# Revit family: 32-70-003-DN50-300
name_source: partatom
category: Pipe Accessories
units: mm (PartAtom-declared; Revit-internal decimal feet)

## family parameters
Always vertical = No
Cut with Voids When Loaded = No
Part Type = Valve - Breaks Into
Round Connector Dimension = Use Diameter
Shared = No
Work Plane-Based = No

## types (10) — shared parameters
32-050-70-016 = DN050_PN16
32-060-70-016 = DN060_PN16
32-065-70-016 = DN065_PN16
32-080-70-0146499 = DN080_PN16
32-100-70-0146499 = DN100_PN16
32-125-70-0146499 = DN125_PN16
32-150-70-0146499 = DN150_PN16
32-200-70-0146499 = DN200_PN16
32-250-70-016 = DN250_PN16
32-300-70-016 = DN300_PN16
Body_Wallthickness = 15 mm  [stored 0.0492126 ft]
Description_ = AVK GATE VALVE, SHORT SPIGOT ENDS
Ftc = 4 mm  [stored 0.0131234 ft]
Name_Height_reference = 10 mm  [stored 0.0328084 ft]
Rib_Height_Reference_3 = 100 mm
Rib_Thickness = 18 mm  [stored 0.0590551 ft]
Search_table = 32-70-003-DN50-300
URL product pages = https://www.avkvalves.com
zero-valued in all types: Bottom_Reference, E

## per-type parameters (varying)
- DN080_PN16: At=70 mm; Body_Height=132 mm; Body_depth=140 mm; Body_width=75 mm; Body_width_ref=90 mm; Bonnet_Flange_Depth=171 mm; Bonnet_Flange_Width=90 mm; Bonnet_Flange_cut=8 mm  [stored 0.0262467 ft]; Bonnet_Flange_thickness=15 mm  [stored 0.0492126 ft]; Bonnet_Height=50 mm; Bonnet_Reference_height=122 mm; Bonnet_Thickness=77 mm; Bt=77 mm; Bt_2=69 mm; CL _Thickness=27 mm  [stored 0.0885827 ft]; CL_Height=75 mm; Cut_Reference=560 mm; D=49 mm; D2=34 mm  [stored 0.111549 ft]; D_ref=50 mm; D_ref_2=46 mm; F=9 mm; F1=10 mm  [stored 0.0328084 ft]; F1_ref=20 mm  [stored 0.0656168 ft]; Fillet_Thickness=6 mm  [stored 0.019685 ft]; Flange_OR=100 mm; Flange_Thickness=19 mm  [stored 0.062336 ft]; Flange_Thickness_cut=30 mm  [stored 0.0984252 ft]; Ftc_reference_height=100 mm; H=282 mm; H1=248 mm; H3=337 mm; H3_ref=55 mm; Horizontal_Flange_width=110 mm; ID=40 mm  [stored 0.131234 ft]; L=280 mm; L1=85 mm; L2=140 mm; L_Dia=80 mm; L_ref=140 mm; Name_Reference=90 mm; Name_Width=38 mm; Neck_H=41 mm  [stored 0.134514 ft]; Neck_T=25 mm  [stored 0.082021 ft]; Neck_T2=23 mm  [stored 0.0754593 ft]; Nominal Diameter (DN)=80 mm; R1tv=1000 mm; R2f=15 mm  [stored 0.0492126 ft]; RF_Dia=66 mm; Rf=183 mm; Rib_Height_Reference_1=120 mm; Rib_Height_Reference_2=110 mm; Rib_Height_Reference_4=85 mm; Rib_Width_1=38 mm; Rib_Width_2=38 mm; Rib_Width_3=38 mm; Rib_depth_1=38 mm; Rib_depth_2=38 mm; Rib_depth_3=38 mm; Rt=333 mm; S=3 mm  [stored 0.00984252 ft]
- DN050_PN16: At=48 mm; Body_Height=101 mm; Body_depth=95 mm; Body_width=72 mm; Body_width_ref=86 mm; Bonnet_Flange_Depth=118 mm; Bonnet_Flange_Width=82 mm; Bonnet_Flange_cut=8 mm  [stored 0.0262467 ft]; Bonnet_Flange_thickness=15 mm  [stored 0.0492126 ft]; Bonnet_Height=41 mm  [stored 0.134514 ft]; Bonnet_Reference_height=91 mm; Bonnet_Thickness=73 mm; Bt=73 mm; Bt_2=66 mm; CL _Thickness=25 mm  [stored 0.082021 ft]; CL_Height=53 mm; Cut_Reference=488 mm; D=33 mm  [stored 0.108268 ft]; D2=29 mm  [stored 0.0951444 ft]; D_ref=35 mm  [stored 0.114829 ft]; D_ref_2=30 mm  [stored 0.0984252 ft]; F=7 mm  [stored 0.0229659 ft]; F1=9 mm; F1_ref=17 mm  [stored 0.0557743 ft]; Fillet_Thickness=6 mm  [stored 0.019685 ft]; Flange_OR=83 mm; Flange_Thickness=19 mm  [stored 0.062336 ft]; Flange_Thickness_cut=29 mm  [stored 0.0951444 ft]; Ftc_reference_height=83 mm; H=241 mm; H1=212 mm; H3=274 mm; H3_ref=33 mm  [stored 0.108268 ft]; Horizontal_Flange_width=66 mm; ID=25 mm  [stored 0.082021 ft]; L=244 mm; L1=72 mm; L2=110 mm; L_Dia=50 mm; L_ref=122 mm; Name_Reference=71 mm; Name_Width=36 mm  [stored 0.11811 ft]; Neck_H=59 mm; Neck_T=23 mm  [stored 0.0754593 ft]; Neck_T2=21 mm; Nominal Diameter (DN)=50 mm; R1tv=825 mm; R2f=15 mm  [stored 0.0492126 ft]; RF_Dia=50 mm; Rf=110 mm; Rib_Height_Reference_1=120 mm; Rib_Height_Reference_2=110 mm; Rib_Height_Reference_4=60 mm; Rib_Width_1=36 mm  [stored 0.11811 ft]; Rib_Width_2=36 mm  [stored 0.11811 ft]; Rib_Width_3=36 mm  [stored 0.11811 ft]; Rib_depth_1=36 mm  [stored 0.11811 ft]; Rib_depth_2=36 mm  [stored 0.11811 ft]; Rib_depth_3=36 mm  [stored 0.11811 ft]; Rt=275 mm; S=3 mm  [stored 0.00984252 ft]
- DN060_PN16: At=50 mm; Body_Height=110 mm; Body_depth=100 mm; Body_width=72 mm; Body_width_ref=86 mm; Bonnet_Flange_Depth=125 mm; Bonnet_Flange_Width=82 mm; Bonnet_Flange_cut=8 mm  [stored 0.0262467 ft]; Bonnet_Flange_thickness=15 mm  [stored 0.0492126 ft]; Bonnet_Height=44 mm  [stored 0.144357 ft]; Bonnet_Reference_height=100 mm; Bonnet_Thickness=73 mm; Bt=73 mm; Bt_2=66 mm; CL _Thickness=25 mm  [stored 0.082021 ft]; CL_Height=55 mm; Cut_Reference=508 mm; D=39 mm  [stored 0.127953 ft]; D2=34 mm  [stored 0.111549 ft]; D_ref=40 mm  [stored 0.131234 ft]; D_ref_2=36 mm  [stored 0.11811 ft]; F=9 mm; F1=10 mm  [stored 0.0328084 ft]; F1_ref=20 mm  [stored 0.0656168 ft]; Fillet_Thickness=6 mm  [stored 0.019685 ft]; Flange_OR=88 mm; Flange_Thickness=19 mm  [stored 0.062336 ft]; Flange_Thickness_cut=29 mm  [stored 0.0951444 ft]; Ftc_reference_height=88 mm; H=271 mm; H1=237 mm; H3=312 mm; H3_ref=41 mm  [stored 0.134514 ft]; Horizontal_Flange_width=82 mm; ID=30 mm  [stored 0.0984252 ft]; L=254 mm; L1=73 mm; L2=120 mm; L_Dia=60 mm; L_ref=127 mm; Name_Reference=85 mm; Name_Width=36 mm  [stored 0.11811 ft]; Neck_H=72 mm; Neck_T=23 mm  [stored 0.0754593 ft]; Neck_T2=21 mm; Nominal Diameter (DN)=60 mm; R1tv=875 mm; R2f=15 mm  [stored 0.0492126 ft]; RF_Dia=55 mm; Rf=137 mm; Rib_Height_Reference_1=120 mm; Rib_Height_Reference_2=110 mm; Rib_Height_Reference_4=68 mm; Rib_Width_1=36 mm  [stored 0.11811 ft]; Rib_Width_2=36 mm  [stored 0.11811 ft]; Rib_Width_3=36 mm  [stored 0.11811 ft]; Rib_depth_1=36 mm  [stored 0.11811 ft]; Rib_depth_2=36 mm  [stored 0.11811 ft]; Rib_depth_3=36 mm  [stored 0.11811 ft]; Rt=292 mm; S=3 mm  [stored 0.00984252 ft]
- DN065_PN16: At=54 mm; Body_Height=115 mm; Body_depth=107 mm; Body_width=72 mm; Body_width_ref=86 mm; Bonnet_Flange_Depth=135 mm; Bonnet_Flange_Width=75 mm; Bonnet_Flange_cut=8 mm  [stored 0.0262467 ft]; Bonnet_Flange_thickness=15 mm  [stored 0.0492126 ft]; Bonnet_Height=46 mm; Bonnet_Reference_height=105 mm; Bonnet_Thickness=73 mm; Bt=73 mm; Bt_2=66 mm; CL _Thickness=25 mm  [stored 0.082021 ft]; CL_Height=59 mm; Cut_Reference=528 mm; D=41 mm  [stored 0.134514 ft]; D2=34 mm  [stored 0.111549 ft]; D_ref=43 mm; D_ref_2=38 mm; F=9 mm; F1=10 mm  [stored 0.0328084 ft]; F1_ref=20 mm  [stored 0.0656168 ft]; Fillet_Thickness=6 mm  [stored 0.019685 ft]; Flange_OR=93 mm; Flange_Thickness=19 mm  [stored 0.062336 ft]; Flange_Thickness_cut=30 mm  [stored 0.0984252 ft]; Ftc_reference_height=93 mm; H=271 mm; H1=237 mm; H3=312 mm; H3_ref=41 mm  [stored 0.134514 ft]; Horizontal_Flange_width=82 mm; ID=33 mm  [stored 0.108268 ft]; L=264 mm; L1=81 mm; L2=130 mm; L_Dia=65 mm; L_ref=132 mm; Name_Reference=96 mm; Name_Width=36 mm  [stored 0.11811 ft]; Neck_H=64 mm; Neck_T=23 mm  [stored 0.0754593 ft]; Neck_T2=21 mm; Nominal Diameter (DN)=65 mm; R1tv=925 mm; R2f=15 mm  [stored 0.0492126 ft]; RF_Dia=59 mm; Rf=137 mm; Rib_Height_Reference_1=120 mm; Rib_Height_Reference_2=110 mm; Rib_Height_Reference_4=75 mm; Rib_Width_1=36 mm  [stored 0.11811 ft]; Rib_Width_2=36 mm  [stored 0.11811 ft]; Rib_Width_3=36 mm  [stored 0.11811 ft]; Rib_depth_1=36 mm  [stored 0.11811 ft]; Rib_depth_2=36 mm  [stored 0.11811 ft]; Rib_depth_3=36 mm  [stored 0.11811 ft]; Rt=308 mm; S=3 mm  [stored 0.00984252 ft]
- DN100_PN16: At=83 mm; Body_Height=148 mm; Body_depth=166 mm; Body_width=80 mm; Body_width_ref=96 mm; Bonnet_Flange_Depth=192 mm; Bonnet_Flange_Width=100 mm; Bonnet_Flange_cut=8 mm  [stored 0.0262467 ft]; Bonnet_Flange_thickness=15 mm  [stored 0.0492126 ft]; Bonnet_Height=55 mm; Bonnet_Reference_height=138 mm; Bonnet_Thickness=82 mm; Bt=82 mm; Bt_2=74 mm; CL _Thickness=29 mm  [stored 0.0951444 ft]; CL_Height=88 mm; Cut_Reference=600 mm; D=59 mm; D2=34 mm  [stored 0.111549 ft]; D_ref=60 mm; D_ref_2=56 mm; F=10 mm  [stored 0.0328084 ft]; F1=11 mm  [stored 0.0360892 ft]; F1_ref=22 mm  [stored 0.0721785 ft]; Fillet_Thickness=6 mm  [stored 0.019685 ft]; Flange_OR=110 mm; Flange_Thickness=19 mm  [stored 0.062336 ft]; Flange_Thickness_cut=30 mm  [stored 0.0984252 ft]; Ftc_reference_height=110 mm; H=305 mm; H1=271 mm; H3=370 mm; H3_ref=65 mm; Horizontal_Flange_width=130 mm; ID=50 mm; L=300 mm; L1=86 mm; L2=150 mm; L_Dia=100 mm; L_ref=150 mm; Name_Reference=101 mm; Name_Width=40 mm  [stored 0.131234 ft]; Neck_H=35 mm  [stored 0.114829 ft]; Neck_T=27 mm  [stored 0.0885827 ft]; Neck_T2=25 mm  [stored 0.082021 ft]; Nominal Diameter (DN)=100 mm; R1tv=1100 mm; R2f=15 mm  [stored 0.0492126 ft]; RF_Dia=78 mm; Rf=217 mm; Rib_Height_Reference_1=120 mm; Rib_Height_Reference_2=110 mm; Rib_Height_Reference_4=90 mm; Rib_Width_1=40 mm  [stored 0.131234 ft]; Rib_Width_2=40 mm  [stored 0.131234 ft]; Rib_Width_3=40 mm  [stored 0.131234 ft]; Rib_depth_1=40 mm  [stored 0.131234 ft]; Rib_depth_2=40 mm  [stored 0.131234 ft]; Rib_depth_3=40 mm  [stored 0.131234 ft]; Rt=367 mm; S=4 mm  [stored 0.0131234 ft]
- DN125_PN16: At=100 mm; Body_Height=137 mm; Body_depth=200 mm; Body_width=90 mm; Body_width_ref=108 mm; Bonnet_Flange_Depth=220 mm; Bonnet_Flange_Width=90 mm; Bonnet_Flange_cut=8 mm  [stored 0.0262467 ft]; Bonnet_Flange_thickness=15 mm  [stored 0.0492126 ft]; Bonnet_Height=63 mm; Bonnet_Reference_height=127 mm; Bonnet_Thickness=92 mm; Bt=92 mm; Bt_2=84 mm; CL _Thickness=34 mm  [stored 0.111549 ft]; CL_Height=105 mm; Cut_Reference=638 mm; D=72 mm; D2=34 mm  [stored 0.111549 ft]; D_ref=73 mm; D_ref_2=69 mm; F=10 mm  [stored 0.0328084 ft]; F1=11 mm  [stored 0.0360892 ft]; F1_ref=22 mm  [stored 0.0721785 ft]; Fillet_Thickness=6 mm  [stored 0.019685 ft]; Flange_OR=125 mm; Flange_Thickness=19 mm  [stored 0.062336 ft]; Flange_Thickness_cut=31 mm  [stored 0.101706 ft]; Ftc_reference_height=125 mm; H=346 mm; H1=312 mm; H3=423 mm; H3_ref=77 mm; Horizontal_Flange_width=154 mm; ID=63 mm; L=319 mm; L1=87 mm; L2=165 mm; L_Dia=125 mm; L_ref=160 mm; Name_Reference=114 mm; Name_Width=45 mm; Neck_H=70 mm; Neck_T=32 mm  [stored 0.104987 ft]; Neck_T2=30 mm  [stored 0.0984252 ft]; Nominal Diameter (DN)=125 mm; R1tv=1250 mm; R2f=15 mm  [stored 0.0492126 ft]; RF_Dia=92 mm; Rf=257 mm; Rib_Height_Reference_1=120 mm; Rib_Height_Reference_2=110 mm; Rib_Height_Reference_4=120 mm; Rib_Width_1=45 mm; Rib_Width_2=45 mm; Rib_Width_3=45 mm; Rib_depth_1=45 mm; Rib_depth_2=45 mm; Rib_depth_3=45 mm; Rt=417 mm; S=5 mm  [stored 0.0164042 ft]
- DN150_PN16: At=121 mm; Body_Height=190 mm; Body_depth=242 mm; Body_width=95 mm; Body_width_ref=114 mm; Bonnet_Flange_Depth=272 mm; Bonnet_Flange_Width=130 mm; Bonnet_Flange_cut=8 mm  [stored 0.0262467 ft]; Bonnet_Flange_thickness=15 mm  [stored 0.0492126 ft]; Bonnet_Height=71 mm; Bonnet_Reference_height=180 mm; Bonnet_Thickness=97 mm; Bt=97 mm; Bt_2=89 mm; CL _Thickness=34 mm  [stored 0.111549 ft]; CL_Height=126 mm; Cut_Reference=700 mm; D=85 mm; D2=34 mm  [stored 0.111549 ft]; D_ref=85 mm; D_ref_2=82 mm; F=10 mm  [stored 0.0328084 ft]; F1=11 mm  [stored 0.0360892 ft]; F1_ref=22 mm  [stored 0.0721785 ft]; Fillet_Thickness=12 mm  [stored 0.0393701 ft]; Flange_OR=142 mm; Flange_Thickness=19 mm  [stored 0.062336 ft]; Flange_Thickness_cut=34 mm  [stored 0.111549 ft]; Ftc_reference_height=142 mm; H=400 mm; H1=366 mm; H3=491 mm; H3_ref=91 mm; Horizontal_Flange_width=182 mm; ID=75 mm; L=350 mm; L1=96 mm; L2=175 mm; L_Dia=150 mm; L_ref=175 mm; Name_Reference=143 mm; Name_Width=48 mm; Neck_H=50 mm; Neck_T=32 mm  [stored 0.104987 ft]; Neck_T2=30 mm  [stored 0.0984252 ft]; Nominal Diameter (DN)=150 mm; R1tv=1420 mm; R2f=30 mm  [stored 0.0984252 ft]; RF_Dia=106 mm; Rf=303 mm; Rib_Height_Reference_1=120 mm; Rib_Height_Reference_2=110 mm; Rib_Height_Reference_4=150 mm; Rib_Width_1=48 mm; Rib_Width_2=48 mm; Rib_Width_3=48 mm; Rib_depth_1=48 mm; Rib_depth_2=48 mm; Rib_depth_3=48 mm; Rt=473 mm; S=5 mm  [stored 0.0164042 ft]
- DN200_PN16: At=165 mm; Body_Height=230 mm; Body_depth=330 mm; Body_width=108 mm; Body_width_ref=130 mm; Bonnet_Flange_Depth=332 mm; Bonnet_Flange_Width=140 mm; Bonnet_Flange_cut=13 mm; Bonnet_Flange_thickness=25 mm  [stored 0.082021 ft]; Bonnet_Height=85 mm; Bonnet_Reference_height=220 mm; Bonnet_Thickness=110 mm; Bt=110 mm; Bt_2=102 mm; CL _Thickness=34 mm  [stored 0.111549 ft]; CL_Height=170 mm; Cut_Reference=800 mm; D=111 mm; D2=34 mm  [stored 0.111549 ft]; D_ref=110 mm; D_ref_2=108 mm; F=12 mm  [stored 0.0393701 ft]; F1=14 mm  [stored 0.0459318 ft]; F1_ref=27 mm  [stored 0.0885827 ft]; Fillet_Thickness=24 mm  [stored 0.0787402 ft]; Flange_OR=170 mm; Flange_Thickness=20 mm  [stored 0.0656168 ft]; Flange_Thickness_cut=35 mm  [stored 0.114829 ft]; Ftc_reference_height=170 mm; H=490 mm; H1=456 mm; H3=608 mm; H3_ref=118 mm; Horizontal_Flange_width=236 mm; ID=100 mm; L=400 mm; L1=110 mm; L2=200 mm; L_Dia=200 mm; L_ref=200 mm; Name_Reference=183 mm; Name_Width=54 mm; Neck_H=56 mm; Neck_T=32 mm  [stored 0.104987 ft]; Neck_T2=30 mm  [stored 0.0984252 ft]; Nominal Diameter (DN)=200 mm; R1tv=1700 mm; R2f=60 mm; RF_Dia=133 mm; Rf=393 mm; Rib_Height_Reference_1=120 mm; Rib_Height_Reference_2=110 mm; Rib_Height_Reference_4=180 mm; Rib_Width_1=54 mm; Rib_Width_2=54 mm; Rib_Width_3=54 mm; Rib_depth_1=54 mm; Rib_depth_2=54 mm; Rib_depth_3=54 mm; Rt=567 mm; S=6 mm  [stored 0.019685 ft]
- DN250_PN16: At=196 mm; Body_Height=320 mm; Body_depth=392 mm; Body_width=132 mm; Body_width_ref=158 mm; Bonnet_Flange_Depth=422 mm; Bonnet_Flange_Width=175 mm; Bonnet_Flange_cut=13 mm; Bonnet_Flange_thickness=25 mm  [stored 0.082021 ft]; Bonnet_Height=100 mm; Bonnet_Reference_height=310 mm; Bonnet_Thickness=135 mm; Bt=135 mm; Bt_2=126 mm; CL _Thickness=46 mm; CL_Height=201 mm; Cut_Reference=900 mm; D=137 mm; D2=47 mm; D_ref=135 mm; D_ref_2=134 mm; F=14 mm  [stored 0.0459318 ft]; F1=16 mm  [stored 0.0524934 ft]; F1_ref=31 mm  [stored 0.101706 ft]; Fillet_Thickness=24 mm  [stored 0.0787402 ft]; Flange_OR=200 mm; Flange_Thickness=22 mm  [stored 0.0721785 ft]; Flange_Thickness_cut=38 mm; Ftc_reference_height=200 mm; H=664 mm; H1=617 mm; H3=801 mm; H3_ref=137 mm; Horizontal_Flange_width=274 mm; ID=125 mm; L=450 mm; L1=131 mm; L2=200 mm; L_Dia=250 mm; L_ref=225 mm; Name_Reference=200 mm; Name_Width=66 mm; Neck_H=96 mm; Neck_T=44 mm  [stored 0.144357 ft]; Neck_T2=42 mm; Nominal Diameter (DN)=250 mm; R1tv=2000 mm; R2f=60 mm; RF_Dia=160 mm; Rf=457 mm; Rib_Height_Reference_1=90 mm; Rib_Height_Reference_2=110 mm; Rib_Height_Reference_4=250 mm; Rib_Width_1=150 mm; Rib_Width_2=150 mm; Rib_Width_3=66 mm; Rib_depth_1=422 mm; Rib_depth_2=66 mm; Rib_depth_3=66 mm; Rt=667 mm; S=6 mm  [stored 0.019685 ft]
- DN300_PN16: At=209 mm; Body_Height=370 mm; Body_depth=418 mm; Body_width=160 mm; Body_width_ref=192 mm; Bonnet_Flange_Depth=448 mm; Bonnet_Flange_Width=200 mm; Bonnet_Flange_cut=18 mm  [stored 0.0590551 ft]; Bonnet_Flange_thickness=35 mm  [stored 0.114829 ft]; Bonnet_Height=114 mm; Bonnet_Reference_height=360 mm; Bonnet_Thickness=163 mm; Bt=163 mm; Bt_2=154 mm; CL _Thickness=60 mm; CL_Height=214 mm; Cut_Reference=1000 mm; D=163 mm; D2=47 mm; D_ref=160 mm; D_ref_2=160 mm; F=14 mm  [stored 0.0459318 ft]; F1=16 mm  [stored 0.0524934 ft]; F1_ref=31 mm  [stored 0.101706 ft]; Fillet_Thickness=24 mm  [stored 0.0787402 ft]; Flange_OR=228 mm; Flange_Thickness=25 mm  [stored 0.082021 ft]; Flange_Thickness_cut=39 mm  [stored 0.127953 ft]; Ftc_reference_height=228 mm; H=740 mm; H1=693 mm; H3=914 mm; H3_ref=174 mm; Horizontal_Flange_width=348 mm; ID=150 mm; L=500 mm; L1=129 mm; L2=200 mm; L_Dia=300 mm; L_ref=250 mm; Name_Reference=300 mm; Name_Width=80 mm; Neck_H=109 mm; Neck_T=58 mm; Neck_T2=56 mm; Nominal Diameter (DN)=300 mm; R1tv=2275 mm; R2f=60 mm; RF_Dia=185 mm; Rf=580 mm; Rib_Height_Reference_1=113 mm; Rib_Height_Reference_2=285 mm; Rib_Height_Reference_4=325 mm; Rib_Width_1=210 mm; Rib_Width_2=210 mm; Rib_Width_3=80 mm; Rib_depth_1=455 mm; Rib_depth_2=455 mm; Rib_depth_3=80 mm; Rt=758 mm; S=7 mm  [stored 0.0229659 ft]

note: [stored X ft] marks values corroborated as IEEE doubles in the binary element streams (Revit-internal decimal feet)

## geometry (parser evidence)
native form markers: Extrusion x1, Sweep x3
no freeform markers — native parametric forms only
